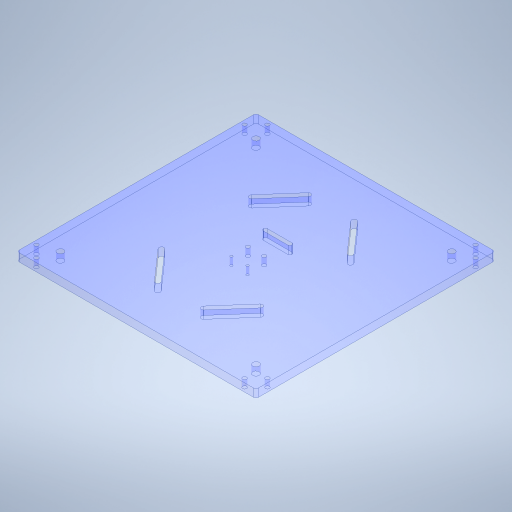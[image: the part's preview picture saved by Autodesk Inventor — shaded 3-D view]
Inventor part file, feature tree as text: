
AUTODESK INVENTOR PART (.ipt)
format: ipt  version: 2023 (Build 270158000, 158)  size: 428,544 bytes
history: native  units: mm
features: extrude x11, sketch x11, plane x1, mirror x1, fillet x1, other x1
ambient origin geometry x8: Origin, YZ Plane, XZ Plane, XY Plane, X Axis, Y Axis, Z Axis, Center Point
bodies: Solid1 (feature_tree)
feature tree (26):
  extrude  "Extrusion1"  Depth=8.1mm
  extrude  "Extrusion2"  Depth=8.1mm
  extrude  "Extrusion3"  Depth=6.0mm
  plane  "Work Plane1"
  mirror  "Mirror1"
  extrude  "Extrusion4"  Depth=55.0mm
  extrude  "Extrusion5"  Depth=55.0mm
  extrude  "Extrusion6"  Depth=6.0mm
  extrude  "Extrusion8"  Depth=6.0mm
  extrude  "Extrusion7"  Depth=50.0mm
  extrude  "Extrusion9"  Depth=10.0mm TaperAngle=0.0deg
  extrude  "Extrusion10"  Depth=5.0mm
  fillet  "Fillet1"  Radius=100.0mm
  extrude  "Extrusion11"  Depth=10.0mm
  sketch  "Sketch1"  dims[d0=8.1mm d1=8.1mm]
  sketch  "Sketch2"  dims[d2=8.1mm d3=8.1mm]
  sketch  "Sketch3"  dims[d4=10.0mm d5=0.0mm d6=6.0mm]
  sketch  "Sketch4"  dims[d7=120.0mm d8=55.0mm]
  sketch  "Sketch5"  dims[d9=120.0mm d10=55.0mm]
  sketch  "Sketch7"  dims[d11=6.0mm d12=148.5mm]
  sketch  "Sketch9"  dims[d13=10.0mm d14=0.0mm d15=6.0mm]
  sketch  "Sketch10"  dims[d16=8.5mm d17=50.0mm]
  sketch  "Sketch11"  dims[d18=10.0mm d19=0.0mm d20=10.0mm d21=0.0mm]
  sketch  "Sketch12"  dims[d22=10.0mm d23=5.0mm d24=100.0mm]
  sketch  "Sketch13"  dims[d25=10.0mm d26=0.0mm d27=21.105mm d28=8.1mm d29=10.0mm d30=10.0mm d31=0.0mm d32=20.0mm d33=3.0mm d34=3.0mm d36=10.0mm d37=0.0mm d38=10.0mm d39=0.0mm d40=10.0mm d41=19.0mm d42=25.0mm d43=5.0mm d44=35.0mm d45=10.0mm d46=0.0mm d47=10.0mm d48=0.0mm d49=2.0mm d50=10.0mm d51=5.0mm d52=10.0mm d53=0.0mm]
  other  "Cut-Extrude14"
